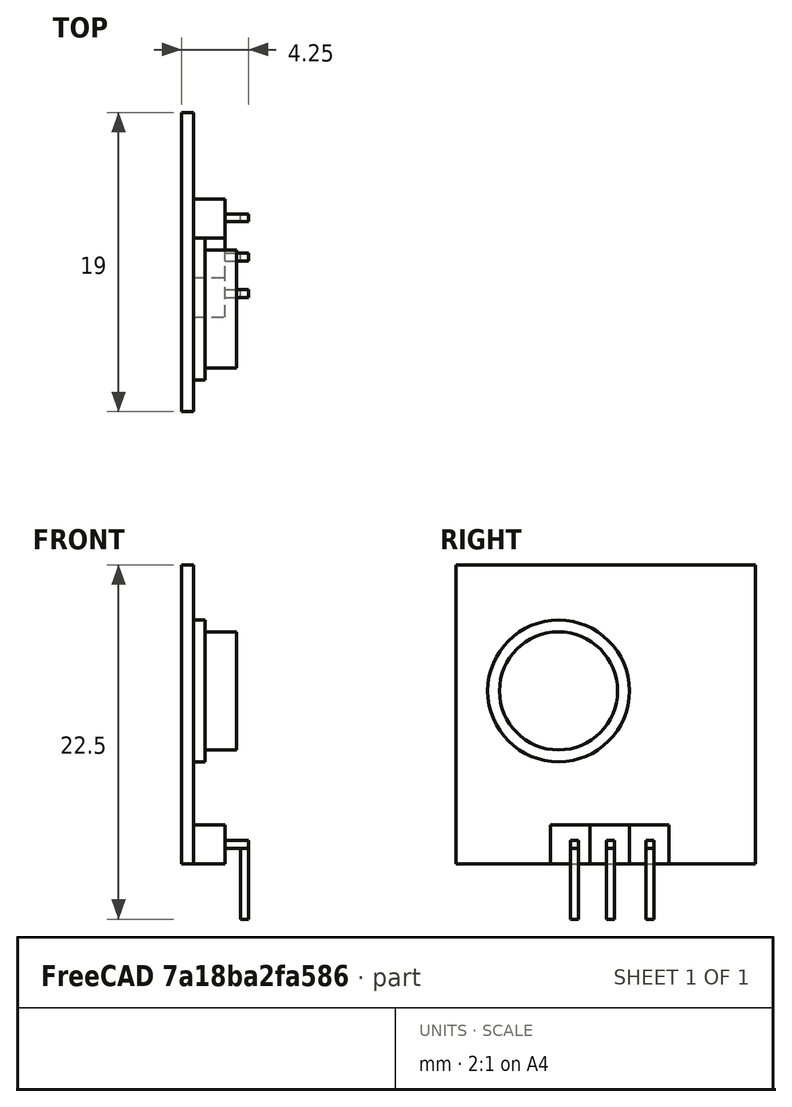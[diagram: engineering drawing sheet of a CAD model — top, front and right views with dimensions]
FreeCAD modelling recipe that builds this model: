
FCSTD DOCUMENT  (FreeCAD 0.16R)
Label: Transmetter_433MHz
License: All rights reserved
LicenseURL: http://en.wikipedia.org/wiki/All_rights_reserved
objects: Part::Box×10, Part::Cylinder×2, Part::Helix×2
note: 14 computed .brp shape members not serialized (recipe doc carries the construction recipe); baked Part::Feature solids carry a one-line shape summary decoded from their .brp

FEATURE [Part::Box] Box  label="Cube"
  Height = 19
  Length = 0.75
  Placement = pos=(0.25,0,0) rot=(0,0,1;0rad)
  Width = 19
FEATURE [Part::Cylinder] Cylinder  label="Cylindre"
  Angle = 360
  Height = 0.75
  Placement = pos=(1,6.5,11) rot=(0,1,0;1.5708rad)
  Radius = 4.5
FEATURE [Part::Cylinder] Cylinder001  label="Cylindre001"
  Angle = 360
  Height = 2
  Placement = pos=(1.75,6.5,11) rot=(0,1,0;1.5708rad)
  Radius = 3.75
FEATURE [Part::Box] Box001  label="Cube001"
  Height = 2.5
  Length = 2
  Placement = pos=(1,6,0) rot=(0,0,1;0rad)
  Width = 2.5
FEATURE [Part::Box] Box002  label="Cube002"
  Height = 2.5
  Length = 2
  Placement = pos=(1,8.5,0) rot=(0,0,1;0rad)
  Width = 2.5
FEATURE [Part::Box] Box003  label="Cube003"
  Height = 2.5
  Length = 2
  Placement = pos=(1,11,0) rot=(0,0,1;0rad)
  Width = 2.5
FEATURE [Part::Box] Box004  label="Cube004"
  Height = 0.5
  Length = 1.5
  Placement = pos=(3,7.25,1) rot=(0,0,1;0rad)
  Width = 0.5
FEATURE [Part::Box] Box005  label="Cube005"
  Height = 4.5
  Length = 0.5
  Placement = pos=(4,7.25,-3.5) rot=(0,0,1;0rad)
  Width = 0.5
FEATURE [Part::Helix] Helix  label="Hélice"
  Angle = 0
  Height = 5
  LocalCoord = 0
  Pitch = 0.5
  Placement = pos=(3.5,17,7) rot=(1,0,0;1.48353rad)
  Radius = 2.5
  Style = 1
FEATURE [Part::Helix] Helix001  label="Hélice001"
  Angle = 0
  Height = 2
  LocalCoord = 0
  Pitch = 0.5
  Placement = pos=(3.5,16,14) rot=(1,0,0;2.60054rad)
  Radius = 2
  Style = 1
FEATURE [Part::Box] Box006  label="Cube006"
  Height = 0.5
  Length = 1.5
  Placement = pos=(3,9.55,1) rot=(0,0,1;0rad)
  Width = 0.5
FEATURE [Part::Box] Box007  label="Cube007"
  Height = 4.5
  Length = 0.5
  Placement = pos=(4,9.55,-3.5) rot=(0,0,1;0rad)
  Width = 0.5
FEATURE [Part::Box] Box008  label="Cube008"
  Height = 0.5
  Length = 1.5
  Placement = pos=(3,12.05,1) rot=(0,0,1;0rad)
  Width = 0.5
FEATURE [Part::Box] Box009  label="Cube009"
  Height = 4.5
  Length = 0.5
  Placement = pos=(4,12.05,-3.5) rot=(0,0,1;0rad)
  Width = 0.5
